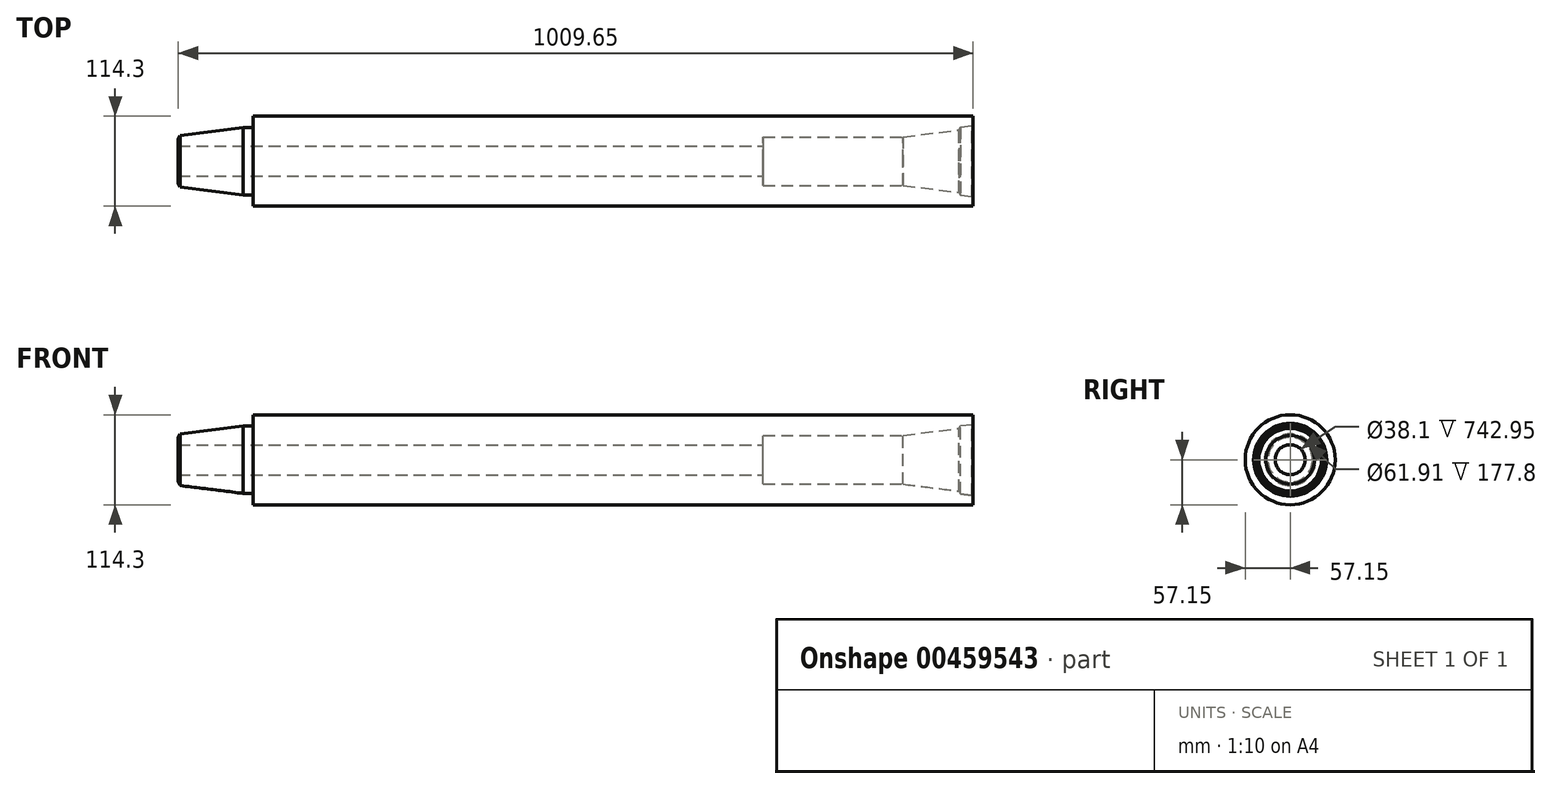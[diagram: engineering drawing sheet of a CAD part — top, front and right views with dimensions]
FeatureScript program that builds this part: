
annotation { "Feature Type Name" : "Feature", "Feature Type Description" : "" }
export const myFeature = defineFeature(function(context is Context, id is Id, definition is map)
    precondition{}
    {
        {
            var Q0;
            Q0=qCreatedBy(makeId("Front.planeOp"),FACE);
            var sketch = newSketch(context, id + "F0", { "sketchPlane" : qUnion([Q0])});
            skLineSegment(sketch, "E0", {"start": v(1009.65, 46.38) * mm, "end": v(1009.65, 57.15) * mm});
            skLineSegment(sketch, "E1", {"start": v(993.78, 43.28) * mm, "end": v(991.78, 39.84) * mm});
            skLineSegment(sketch, "E2", {"start": v(993.78, 43.28) * mm, "end": v(1008.38, 45.1) * mm});
            skLineSegment(sketch, "E3", {"start": v(1008.38, 45.1) * mm, "end": v(1009.65, 46.38) * mm});
            skLineSegment(sketch, "E4", {"start": v(82.55, 42.74) * mm, "end": v(2.55, 32.74) * mm});
            skLineSegment(sketch, "E5", {"start": v(0, 28.32) * mm, "end": v(0, 19.05) * mm});
            skLineSegment(sketch, "E6", {"start": v(0, 28.32) * mm, "end": v(2.55, 32.74) * mm});
            skLineSegment(sketch, "E7", {"start": v(95.25, 57.15) * mm, "end": v(95.25, 42.74) * mm});
            skLineSegment(sketch, "E8", {"start": v(1009.65, 0) * mm, "end": v(0, 0) * mm});
            skLineSegment(sketch, "E9", {"start": v(742.95, 19.05) * mm, "end": v(0, 19.05) * mm});
            skLineSegment(sketch, "E10", {"start": v(991.78, 39.84) * mm, "end": v(920.75, 30.96) * mm});
            skLineSegment(sketch, "E11", {"start": v(920.75, 30.96) * mm, "end": v(742.95, 30.96) * mm});
            skLineSegment(sketch, "E12", {"start": v(742.95, 19.05) * mm, "end": v(742.95, 30.96) * mm});
            skLineSegment(sketch, "E13", {"start": v(1009.65, 57.15) * mm, "end": v(95.25, 57.15) * mm});
            skLineSegment(sketch, "E14", {"start": v(82.55, 42.74) * mm, "end": v(95.25, 42.74) * mm});
            skLineSegment(sketch, "E15", {"start": v(920.75, 57.15) * mm, "end": v(101.6, 57.15) * mm});
            skSolve(sketch);
        }
        {
            var Q0;
            Q0 = qSketchRegion(id + "F0", true);
            var Q1;
            Q1=sQuery(id+"F0.wireOp",EDGE,"E8");
            revolve(context, id + "F1", {"surfaceOperationType" : NewSurfaceOperationType.NEW, "entities" : qUnion([Q0]), "axis" : qUnion([Q1]), "revolveType" : RevolveType.FULL});
        }
    });
